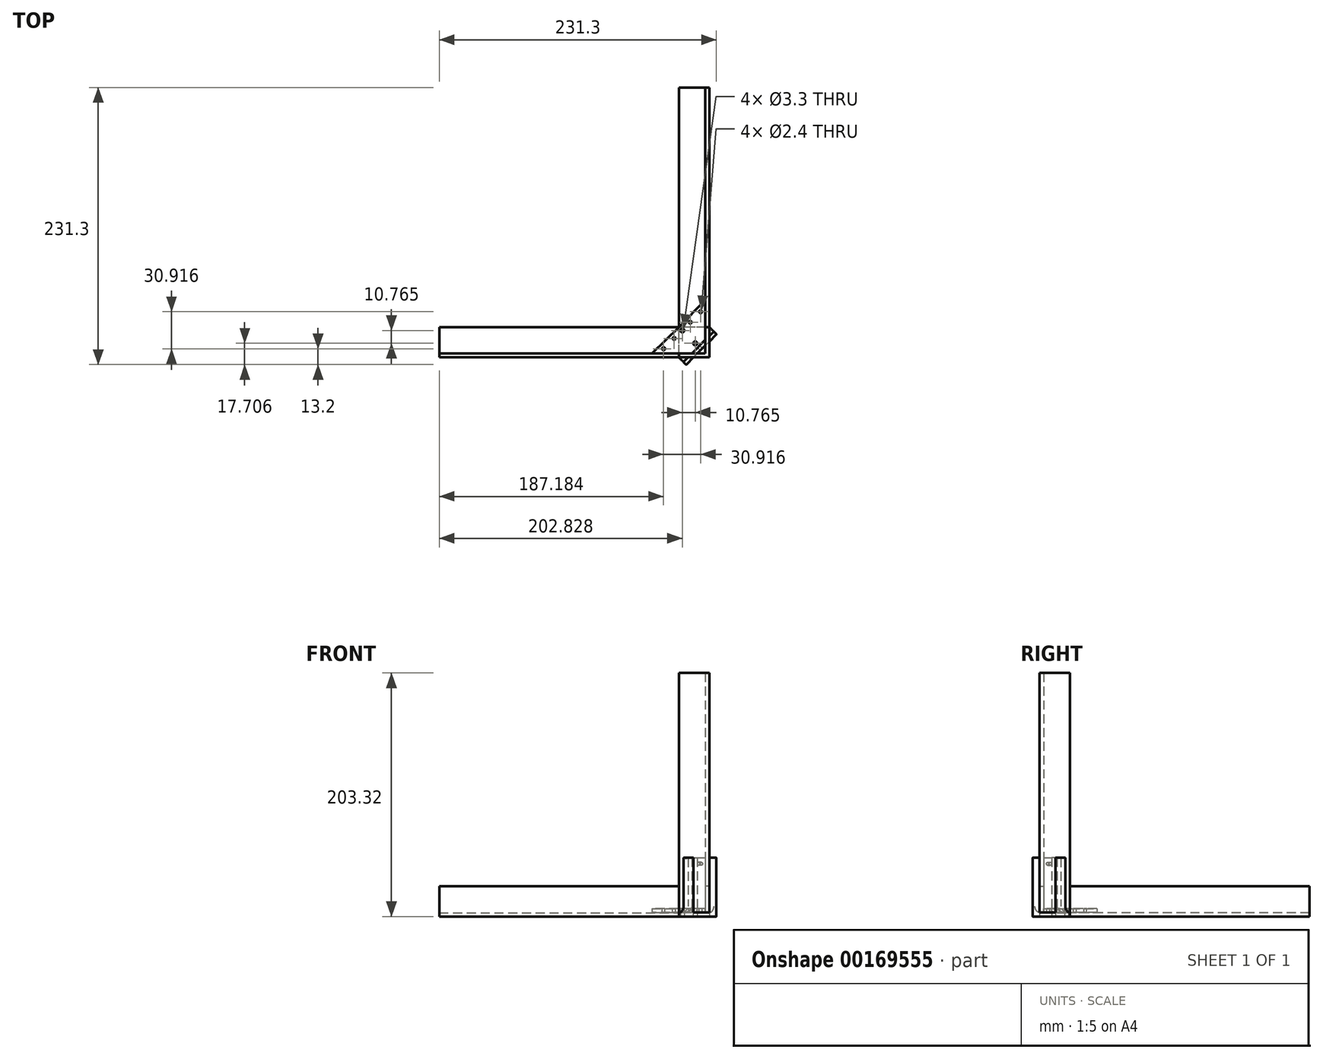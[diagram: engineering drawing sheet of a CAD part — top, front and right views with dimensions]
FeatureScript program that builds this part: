
annotation { "Feature Type Name" : "Feature", "Feature Type Description" : "" }
export const myFeature = defineFeature(function(context is Context, id is Id, definition is map)
    precondition{}
    {
        {
            assignVariable(context, id + "F0", {"name" : "EdgeLWidth", "anyValue" : 25.3 * mm});
        }
        {
            assignVariable(context, id + "F1", {"name" : "HolderLWidth", "anyValue" : 49 * mm});
        }
        {
            assignVariable(context, id + "F2", {"name" : "HolderLThickness", "anyValue" : 3.3 * mm});
        }
        {
            var Q0;
            Q0=qCreatedBy(makeId("Top.planeOp"),FACE);
            var sketch = newSketch(context, id + "F3", { "sketchPlane" : qUnion([Q0])});
            skLineSegment(sketch, "E0", {"start": v(-3.2, 9.89) * mm, "end": v(-6.54, 6.54) * mm});
            skLineSegment(sketch, "E1", {"start": v(-8.88, 8.88) * mm, "end": v(-3.2, 14.56) * mm});
            skLineSegment(sketch, "E2", {"start": v(-3.2, 14.56) * mm, "end": v(-3.2, 9.89) * mm});
            skLineSegment(sketch, "E3", {"start": v(0, 13.09) * mm, "end": v(0, 17.76) * mm});
            skLineSegment(sketch, "E4", {"start": v(0, 17.76) * mm, "end": v(3.77, 21.53) * mm});
            skLineSegment(sketch, "E5", {"start": v(3.77, 21.53) * mm, "end": v(6.1, 19.2) * mm});
            skLineSegment(sketch, "E6", {"start": v(6.1, 19.2) * mm, "end": v(0, 13.09) * mm});
            skLineSegment(sketch, "E7", {"start": v(0, 0) * mm, "end": v(-77.69, 77.69) * mm, "construction": true});
            skLineSegment(sketch, "E8", {"start": v(-77.76, 0) * mm, "end": v(0, 0) * mm, "construction": true});
            skLineSegment(sketch, "E9", {"start": v(0, 0) * mm, "end": v(0, 78.06) * mm, "construction": true});
            skLineSegment(sketch, "E10", {"start": v(6.1, 19.2) * mm, "end": v(-6.54, 6.54) * mm});
            skLineSegment(sketch, "E11.MirrorCS", {"start": v(-19.2, -6.1) * mm, "end": v(-13.09, 0) * mm});
            skLineSegment(sketch, "E12.MirrorCS", {"start": v(-9.89, 3.2) * mm, "end": v(-6.54, 6.54) * mm});
            skLineSegment(sketch, "E13.MirrorCS", {"start": v(-17.76, 0) * mm, "end": v(-21.53, -3.77) * mm});
            skLineSegment(sketch, "E14.MirrorCS", {"start": v(-8.88, 8.88) * mm, "end": v(-14.56, 3.2) * mm});
            skLineSegment(sketch, "E15.MirrorCS", {"start": v(-13.09, 0) * mm, "end": v(-17.76, 0) * mm});
            skLineSegment(sketch, "E16.MirrorCS", {"start": v(-21.53, -3.77) * mm, "end": v(-19.2, -6.1) * mm});
            skLineSegment(sketch, "E17.MirrorCS", {"start": v(-19.2, -6.1) * mm, "end": v(-6.54, 6.54) * mm});
            skLineSegment(sketch, "E18.MirrorCS", {"start": v(-14.56, 3.2) * mm, "end": v(-9.89, 3.2) * mm});
            skPoint(sketch, "E19", {"position": v(-11.7, 11.7) * mm});
            skPoint(sketch, "E20", {"position": v(-22.47, 22.47) * mm});
            skLineSegment(sketch, "E21", {"start": v(3.77, 21.53) * mm, "end": v(0, 25.3) * mm});
            skLineSegment(sketch, "E22", {"start": v(0, 25.3) * mm, "end": v(-25.3, 25.3) * mm});
            skLineSegment(sketch, "E23", {"start": v(-25.3, 25.3) * mm, "end": v(-25.3, 0) * mm});
            skLineSegment(sketch, "E24", {"start": v(-25.3, 0) * mm, "end": v(-21.53, -3.77) * mm});
            skSolve(sketch);
        }
        {
            var Q0;
            Q0=qSketchRegion(id+"F3",true);
            extrude(context, id + "F4", {"entities" : qUnion([Q0]), "depth" : getVariable(context, 'HolderLThickness')});
        }
        {
            var Q0;
            {var subQ0=sQuery(id+"F3.wireOp",EDGE,"E3");Q0=makeQuery(id+"F3.imprint","IMPRINT",FACE,{"disambiguationData":[TD([[makeQuery(id+"F3.imprint","IMPRINT",EDGE,{"derivedFrom":subQ0}),-1.0]])]});}
            var Q1;
            Q1=makeQuery(id+"F3.imprint","IMPRINT",FACE,{"disambiguationData":[TD([[makeQuery(id+"F3.imprint","IMPRINT",EDGE,{"derivedFrom":sQuery(id+"F3.wireOp",EDGE,"E1")}),-1.0]])]});
            var Q2;
            Q2=makeQuery(id+"F3.imprint","IMPRINT",FACE,{"disambiguationData":[TD([[makeQuery(id+"F3.imprint","IMPRINT",EDGE,{"derivedFrom":sQuery(id+"F3.wireOp",EDGE,"E13.MirrorCS")}),1.0]])]});
            extrude(context, id + "F5", {"entities" : qUnion([Q0, Q1, Q2]), "operationType" : NewBodyOperationType.ADD, "depth" : getVariable(context, 'HolderLWidth')});
        }
        {
            var Q0;
            Q0=sQuery(id+"F3.wireOp",VERTEX,"E19");
            var Q1;
            Q1=sQuery(id+"F3.wireOp",VERTEX,"E20");
            var Q2;
            Q2=makeQuery(id+"F4.opExtrude","SWEPT_BODY",BODY,{"disambiguationData":[OSD([sQuery(id+"F3.wireOp",EDGE,"E5"),sQuery(id+"F3.wireOp",EDGE,"o0lL32gh-OSn4-Vle3-xUkx-KtaRwmzb5psM"),sQuery(id+"F3.wireOp",EDGE,"DVCsqTKq-KYus-YFW3-ZN70-3ISmhOG0B1KU"),sQuery(id+"F3.wireOp",EDGE,"E10"),sQuery(id+"F3.wireOp",EDGE,"bed3d973-7b21-4a2b-b050-399250b5e04a2.MirrorCS"),sQuery(id+"F3.wireOp",EDGE,"bed3d973-7b21-4a2b-b050-399250b5e04a6.MirrorCS"),sQuery(id+"F3.wireOp",EDGE,"E16.MirrorCS"),sQuery(id+"F3.wireOp",EDGE,"E17.MirrorCS")])]});
            hole(context, id + "F6", {"style" : HoleStyle.SIMPLE, "endStyle" : HoleEndStyle.THROUGH, "oppositeDirection" : true, "standardTappedOrClearance" : lookupTablePath({ "standard" : "ISO", "fit" : "Normal", "size" : "M3", "type" : "Clearance" }), "standardBlindInLast" : lookupTablePath({ "fit" : "Standard", "standard" : "ISO", "size" : "M3", "type" : "Clearance" }), "holeDiameter" : 3.3 * mm, "startFromSketch" : true, "locations" : qUnion([Q0, Q1]), "scope" : qUnion([Q2]), "isTappedThrough" : true});
        }
        {
            var Q0;
            Q0=makeQuery(id+"F5.opExtrude","SWEPT_FACE",FACE,{"disambiguationData":[OSD([sQuery(id+"F3.wireOp",EDGE,"E1"),sQuery(id+"F3.wireOp",EDGE,"E14.MirrorCS")])]});
            var sketch = newSketch(context, id + "F7", { "sketchPlane" : qUnion([Q0])});
            skLineSegment(sketch, "E25", {"start": v(0, 49) * mm, "end": v(0, 0) * mm, "construction": true});
            skPoint(sketch, "E26", {"position": v(0, 44) * mm});
            skSolve(sketch);
        }
        {
            var Q0;
            Q0=sQuery(id+"F7.wireOp",VERTEX,"E26");
            var Q1;
            Q1=makeQuery(id+"F4.opExtrude","SWEPT_BODY",BODY,{"disambiguationData":[OSD([sQuery(id+"F3.wireOp",EDGE,"E5"),sQuery(id+"F3.wireOp",EDGE,"o0lL32gh-OSn4-Vle3-xUkx-KtaRwmzb5psM"),sQuery(id+"F3.wireOp",EDGE,"DVCsqTKq-KYus-YFW3-ZN70-3ISmhOG0B1KU"),sQuery(id+"F3.wireOp",EDGE,"E10"),sQuery(id+"F3.wireOp",EDGE,"bed3d973-7b21-4a2b-b050-399250b5e04a2.MirrorCS"),sQuery(id+"F3.wireOp",EDGE,"bed3d973-7b21-4a2b-b050-399250b5e04a6.MirrorCS"),sQuery(id+"F3.wireOp",EDGE,"E16.MirrorCS"),sQuery(id+"F3.wireOp",EDGE,"E17.MirrorCS")])]});
            hole(context, id + "F8", {"style" : HoleStyle.SIMPLE, "endStyle" : HoleEndStyle.THROUGH, "standardTappedOrClearance" : lookupTablePath({ "standard" : "ISO", "engagement" : "75%", "pitch" : "0.6 mm", "size" : "M3", "type" : "Tapped" }), "standardBlindInLast" : lookupTablePath({ "standard" : "ISO", "engagement" : "75%", "pitch" : "0.6 mm", "size" : "M3", "type" : "Tapped" }), "holeDiameter" : 2.4 * mm, "startFromSketch" : true, "locations" : qUnion([Q0]), "scope" : qUnion([Q1]), "isTappedThrough" : true, "showTappedDepth" : true});
        }
        {
            var Q0;
            {var subQ0=sQuery(id+"F3.wireOp",EDGE,"E10");var subQ1=sQuery(id+"F3.wireOp",EDGE,"E5");Q0=makeQuery(id+"F5.boolean.opBoolean","MERGE",EDGE,{"derivedFrom":[makeQuery(id+"F4.opExtrude","SWEPT_EDGE",EDGE,{"disambiguationData":[OSD([subQ1,subQ0])]}),makeQuery(id+"F5.opExtrude","SWEPT_EDGE",EDGE,{"disambiguationData":[OSD([subQ1,subQ0])]})]});}
            var Q1;
            Q1=makeQuery(id+"F5.opExtrude","SWEPT_EDGE",EDGE,{"disambiguationData":[OSD([sQuery(id+"F3.wireOp",EDGE,"E4"),sQuery(id+"F3.wireOp",EDGE,"E5"),sQuery(id+"F3.wireOp",EDGE,"o0lL32gh-OSn4-Vle3-xUkx-KtaRwmzb5psM")])]});
            var Q2;
            Q2=makeQuery(id+"F5.opExtrude","CAP_EDGE",EDGE,{"disambiguationData":[OSD([sQuery(id+"F3.wireOp",EDGE,"E5")])],"isStart":false});
            var Q3;
            Q3=makeQuery(id+"F5.opExtrude","CAP_EDGE",EDGE,{"disambiguationData":[OSD([sQuery(id+"F3.wireOp",EDGE,"E10")])],"isStart":false});
            var Q4;
            Q4=makeQuery(id+"F5.opExtrude","CAP_EDGE",EDGE,{"disambiguationData":[OSD([sQuery(id+"F3.wireOp",EDGE,"E4")])],"isStart":false});
            var Q5;
            Q5=makeQuery(id+"F5.opExtrude","CAP_EDGE",EDGE,{"disambiguationData":[OSD([sQuery(id+"F3.wireOp",EDGE,"E17.MirrorCS")])],"isStart":false});
            var Q6;
            Q6=makeQuery(id+"F5.opExtrude","CAP_EDGE",EDGE,{"disambiguationData":[OSD([sQuery(id+"F3.wireOp",EDGE,"E13.MirrorCS")])],"isStart":false});
            var Q7;
            Q7=makeQuery(id+"F5.opExtrude","CAP_EDGE",EDGE,{"disambiguationData":[OSD([sQuery(id+"F3.wireOp",EDGE,"E16.MirrorCS")])],"isStart":false});
            var Q8;
            {var subQ0=sQuery(id+"F3.wireOp",EDGE,"E17.MirrorCS");var subQ1=sQuery(id+"F3.wireOp",EDGE,"E16.MirrorCS");Q8=makeQuery(id+"F5.boolean.opBoolean","MERGE",EDGE,{"derivedFrom":[makeQuery(id+"F4.opExtrude","SWEPT_EDGE",EDGE,{"disambiguationData":[OSD([subQ1,subQ0])]}),makeQuery(id+"F5.opExtrude","SWEPT_EDGE",EDGE,{"disambiguationData":[OSD([subQ1,subQ0])]})]});}
            var Q9;
            Q9=makeQuery(id+"F5.opExtrude","SWEPT_EDGE",EDGE,{"disambiguationData":[OSD([sQuery(id+"F3.wireOp",EDGE,"bed3d973-7b21-4a2b-b050-399250b5e04a2.MirrorCS"),sQuery(id+"F3.wireOp",EDGE,"E13.MirrorCS"),sQuery(id+"F3.wireOp",EDGE,"E16.MirrorCS")])]});
            fillet(context, id + "F9", {"entities" : qUnion([Q0, Q1, Q2, Q3, Q4, Q5, Q6, Q7, Q8, Q9]), "radius" : .25 * mm, "tangentPropagation" : true, "allowEdgeOverflow" : false});
        }
        {
            var Q0;
            Q0=makeQuery(id+"F4.opExtrude","CAP_FACE",FACE,{"disambiguationData":[OSD([sQuery(id+"F3.wireOp",EDGE,"E5"),sQuery(id+"F3.wireOp",EDGE,"o0lL32gh-OSn4-Vle3-xUkx-KtaRwmzb5psM"),sQuery(id+"F3.wireOp",EDGE,"DVCsqTKq-KYus-YFW3-ZN70-3ISmhOG0B1KU"),sQuery(id+"F3.wireOp",EDGE,"E10"),sQuery(id+"F3.wireOp",EDGE,"bed3d973-7b21-4a2b-b050-399250b5e04a2.MirrorCS"),sQuery(id+"F3.wireOp",EDGE,"bed3d973-7b21-4a2b-b050-399250b5e04a6.MirrorCS"),sQuery(id+"F3.wireOp",EDGE,"E16.MirrorCS"),sQuery(id+"F3.wireOp",EDGE,"E17.MirrorCS")])],"isStart":false});
            var sketch = newSketch(context, id + "F10", { "sketchPlane" : qUnion([Q0])});
            skLineSegment(sketch, "E27", {"start": v(0, 0) * mm, "end": v(0, 25.3) * mm});
            skLineSegment(sketch, "E28", {"start": v(-3.2, 25.3) * mm, "end": v(-3.2, 3.2) * mm});
            skLineSegment(sketch, "E29", {"start": v(-3.2, 3.2) * mm, "end": v(-25.3, 3.2) * mm});
            skLineSegment(sketch, "E30", {"start": v(-25.3, 3.2) * mm, "end": v(-25.3, 0) * mm});
            skLineSegment(sketch, "E31", {"start": v(-25.3, 0) * mm, "end": v(0, 0) * mm});
            skLineSegment(sketch, "E32", {"start": v(-3.2, 25.3) * mm, "end": v(0, 25.3) * mm});
            skSolve(sketch);
        }
        {
            var Q0;
            Q0=qSketchRegion(id+"F10",true);
            extrude(context, id + "F11", {"entities" : qUnion([Q0]), "depth" : 200 * mm});
        }
        {
            var Q0;
            Q0=qCreatedBy(makeId("Right.planeOp"),FACE);
            var sketch = newSketch(context, id + "F12", { "sketchPlane" : qUnion([Q0])});
            skLineSegment(sketch, "E33", {"start": v(0, -0.02) * mm, "end": v(0, 25.28) * mm});
            skLineSegment(sketch, "E34", {"start": v(0, 25.28) * mm, "end": v(3.2, 25.28) * mm});
            skLineSegment(sketch, "E35", {"start": v(3.2, 25.28) * mm, "end": v(3.2, 3.18) * mm});
            skLineSegment(sketch, "E36", {"start": v(3.2, 3.18) * mm, "end": v(25.3, 3.18) * mm});
            skLineSegment(sketch, "E37", {"start": v(25.3, 3.18) * mm, "end": v(25.3, -0.02) * mm});
            skLineSegment(sketch, "E38", {"start": v(0, -0.02) * mm, "end": v(25.3, -0.02) * mm});
            skSolve(sketch);
        }
        {
            var Q0;
            Q0=qSketchRegion(id+"F12",true);
            extrude(context, id + "F13", {"entities" : qUnion([Q0]), "oppositeDirection" : true, "depth" : 200 * mm});
        }
        {
            var Q0;
            Q0=makeQuery(id+"F13.opExtrude","SWEPT_BODY",BODY,{"disambiguationData":[OSD([sQuery(id+"F12.wireOp",EDGE,"E33"),sQuery(id+"F12.wireOp",EDGE,"E34"),sQuery(id+"F12.wireOp",EDGE,"E35"),sQuery(id+"F12.wireOp",EDGE,"E36"),sQuery(id+"F12.wireOp",EDGE,"E37"),sQuery(id+"F12.wireOp",EDGE,"E38")])]});
            var Q1;
            Q1=makeQuery(id+"F13.opExtrude","SWEPT_EDGE",EDGE,{"disambiguationData":[OSD([sQuery(id+"F12.wireOp",EDGE,"E36"),sQuery(id+"F12.wireOp",EDGE,"E37")])]});
            transform(context, id + "F14", {"entities" : qUnion([Q0]), "transformType" : TransformType.TRANSLATION_3D, "dx" : -getVariable(context, 'EdgeLWidth'), "dy" : 0 * mm, "dz" : 0 * mm, "makeCopy" : false});
        }
        {
            var Q0;
            Q0=sQuery(id+"F3.wireOp",EDGE,"E7");
            var Q1;
            Q1=makeQuery(id+"F11.opExtrude","SWEPT_EDGE",EDGE,{"disambiguationData":[OSD([sQuery(id+"F10.wireOp",EDGE,"E27"),sQuery(id+"F10.wireOp",EDGE,"E31")])]});
            cPlane(context, id + "F15", {"entities" : qUnion([Q0, Q1]), "cplaneType" : CPlaneType.LINE_ANGLE, "offset" : 25 * mm, "angle" : 180 * degree, "width" : 150 * mm, "height" : 150 * mm});
        }
        {
            var Q0;
            Q0=makeQuery(id+"F13.opExtrude","SWEPT_BODY",BODY,{"disambiguationData":[OSD([sQuery(id+"F12.wireOp",EDGE,"E33"),sQuery(id+"F12.wireOp",EDGE,"E34"),sQuery(id+"F12.wireOp",EDGE,"E35"),sQuery(id+"F12.wireOp",EDGE,"E36"),sQuery(id+"F12.wireOp",EDGE,"E37"),sQuery(id+"F12.wireOp",EDGE,"E38")])]});
            var Q1;
            Q1=qCreatedBy(id+"F15.planeOp",FACE);
            mirror(context, id + "F16", {"entities" : qUnion([Q0]), "mirrorPlane" : qUnion([Q1])});
        }
        {
            var Q0;
            Q0=makeQuery(id+"F4.opExtrude","CAP_FACE",FACE,{"disambiguationData":[OSD([sQuery(id+"F3.wireOp",EDGE,"E5"),sQuery(id+"F3.wireOp",EDGE,"E10"),sQuery(id+"F3.wireOp",EDGE,"E16.MirrorCS"),sQuery(id+"F3.wireOp",EDGE,"E17.MirrorCS"),sQuery(id+"F3.wireOp",EDGE,"E21"),sQuery(id+"F3.wireOp",EDGE,"E22"),sQuery(id+"F3.wireOp",EDGE,"E23"),sQuery(id+"F3.wireOp",EDGE,"E24")])],"isStart":false});
            var sketch = newSketch(context, id + "F17", { "sketchPlane" : qUnion([Q0])});
            skLineSegment(sketch, "E39", {"start": v(-14.56, 3.2) * mm, "end": v(-47.94, 3.2) * mm});
            skLineSegment(sketch, "E40", {"start": v(-47.94, 3.2) * mm, "end": v(-25.3, 25.3) * mm});
            skLineSegment(sketch, "E41", {"start": v(-8.88, 8.88) * mm, "end": v(-14.56, 3.2) * mm});
            skLineSegment(sketch, "E42.MirrorCS", {"start": v(-8.88, 8.88) * mm, "end": v(-3.2, 14.56) * mm});
            skLineSegment(sketch, "E43.MirrorCS", {"start": v(-3.2, 14.56) * mm, "end": v(-3.2, 47.94) * mm});
            skLineSegment(sketch, "E44.MirrorCS", {"start": v(-3.2, 47.94) * mm, "end": v(-25.3, 25.3) * mm});
            skSolve(sketch);
        }
        {
            var Q0;
            Q0 = qSketchRegion(id + "F17", true);
            extrude(context, id + "F18", {"entities" : qUnion([Q0]), "depth" : getVariable(context, 'HolderLThickness')});
        }
        {
            var Q0;
            Q0=makeQuery(id+"F18.opExtrude","CAP_FACE",FACE,{"disambiguationData":[OSD([sQuery(id+"F17.wireOp",EDGE,"E39"),sQuery(id+"F17.wireOp",EDGE,"E40"),sQuery(id+"F17.wireOp",EDGE,"E41"),sQuery(id+"F17.wireOp",EDGE,"E42.MirrorCS"),sQuery(id+"F17.wireOp",EDGE,"E43.MirrorCS"),sQuery(id+"F17.wireOp",EDGE,"E44.MirrorCS")])],"isStart":false});
            var sketch = newSketch(context, id + "F19", { "sketchPlane" : qUnion([Q0])});
            skPoint(sketch, "E45", {"position": v(-22.47, 22.47) * mm});
            skPoint(sketch, "E46", {"position": v(-11.7, 11.7) * mm});
            skPoint(sketch, "E47", {"position": v(-29.3, 15.8) * mm});
            skPoint(sketch, "E48", {"position": v(-38.12, 7.2) * mm});
            skPoint(sketch, "E49.MirrorP", {"position": v(-15.8, 29.3) * mm});
            skPoint(sketch, "E50.MirrorP", {"position": v(-7.2, 38.12) * mm});
            skSolve(sketch);
        }
        {
            var Q0;
            Q0=sQuery(id+"F19.wireOp",VERTEX,"E45");
            var Q1;
            Q1=sQuery(id+"F19.wireOp",VERTEX,"E46");
            var Q2;
            Q2=makeQuery(id+"F18.opExtrude","SWEPT_BODY",BODY,{"disambiguationData":[OSD([sQuery(id+"F17.wireOp",EDGE,"E39"),sQuery(id+"F17.wireOp",EDGE,"E40"),sQuery(id+"F17.wireOp",EDGE,"E41"),sQuery(id+"F17.wireOp",EDGE,"E42.MirrorCS"),sQuery(id+"F17.wireOp",EDGE,"E43.MirrorCS"),sQuery(id+"F17.wireOp",EDGE,"E44.MirrorCS")])]});
            hole(context, id + "F20", {"style" : HoleStyle.SIMPLE, "endStyle" : HoleEndStyle.THROUGH, "standardTappedOrClearance" : lookupTablePath({ "standard" : "ISO", "fit" : "Normal", "size" : "M3", "type" : "Clearance" }), "standardBlindInLast" : lookupTablePath({ "fit" : "Standard", "standard" : "ISO", "size" : "M3", "type" : "Clearance" }), "holeDiameter" : 3.3 * mm, "startFromSketch" : true, "locations" : qUnion([Q0, Q1]), "scope" : qUnion([Q2]), "isTappedThrough" : true});
        }
        {
            var Q0;
            Q0=sQuery(id+"F19.wireOp",VERTEX,"E48");
            var Q1;
            Q1=sQuery(id+"F19.wireOp",VERTEX,"E47");
            var Q2;
            Q2=sQuery(id+"F19.wireOp",VERTEX,"E49.MirrorP");
            var Q3;
            Q3=sQuery(id+"F19.wireOp",VERTEX,"E50.MirrorP");
            var Q4;
            Q4=makeQuery(id+"F18.opExtrude","SWEPT_BODY",BODY,{"disambiguationData":[OSD([sQuery(id+"F17.wireOp",EDGE,"E39"),sQuery(id+"F17.wireOp",EDGE,"E40"),sQuery(id+"F17.wireOp",EDGE,"E41"),sQuery(id+"F17.wireOp",EDGE,"E42.MirrorCS"),sQuery(id+"F17.wireOp",EDGE,"E43.MirrorCS"),sQuery(id+"F17.wireOp",EDGE,"E44.MirrorCS")])]});
            hole(context, id + "F21", {"style" : HoleStyle.SIMPLE, "endStyle" : HoleEndStyle.THROUGH, "standardTappedOrClearance" : lookupTablePath({ "standard" : "ISO", "engagement" : "75%", "pitch" : "0.6 mm", "size" : "M3", "type" : "Tapped" }), "standardBlindInLast" : lookupTablePath({ "standard" : "ISO", "engagement" : "75%", "pitch" : "0.6 mm", "size" : "M3", "type" : "Tapped" }), "holeDiameter" : 2.4 * mm, "locations" : qUnion([Q0, Q1, Q2, Q3]), "scope" : qUnion([Q4]), "isTappedThrough" : true, "showTappedDepth" : true});
        }
        {
            var Q0;
            Q0=makeQuery(id+"F18.opExtrude","CAP_EDGE",EDGE,{"disambiguationData":[OSD([sQuery(id+"F17.wireOp",EDGE,"E41"),sQuery(id+"F17.wireOp",EDGE,"E42.MirrorCS")])],"isStart":true});
            var Q1;
            Q1=makeQuery(id+"F5.boolean.opBoolean","INTERSECT",EDGE,{"derivedFrom":[makeQuery(id+"F4.opExtrude","CAP_FACE",FACE,{"disambiguationData":[OSD([sQuery(id+"F3.wireOp",EDGE,"E5"),sQuery(id+"F3.wireOp",EDGE,"E10"),sQuery(id+"F3.wireOp",EDGE,"E16.MirrorCS"),sQuery(id+"F3.wireOp",EDGE,"E17.MirrorCS"),sQuery(id+"F3.wireOp",EDGE,"E21"),sQuery(id+"F3.wireOp",EDGE,"E22"),sQuery(id+"F3.wireOp",EDGE,"E23"),sQuery(id+"F3.wireOp",EDGE,"E24")])],"isStart":false}),makeQuery(id+"F5.opExtrude","SWEPT_FACE",FACE,{"disambiguationData":[OSD([sQuery(id+"F3.wireOp",EDGE,"E1"),sQuery(id+"F3.wireOp",EDGE,"E14.MirrorCS")])]})]});
            var Q2;
            Q2=makeQuery(id+"F5.boolean.opBoolean","INTERSECT",EDGE,{"derivedFrom":[makeQuery(id+"F4.opExtrude","CAP_FACE",FACE,{"disambiguationData":[OSD([sQuery(id+"F3.wireOp",EDGE,"E5"),sQuery(id+"F3.wireOp",EDGE,"E10"),sQuery(id+"F3.wireOp",EDGE,"E16.MirrorCS"),sQuery(id+"F3.wireOp",EDGE,"E17.MirrorCS"),sQuery(id+"F3.wireOp",EDGE,"E21"),sQuery(id+"F3.wireOp",EDGE,"E22"),sQuery(id+"F3.wireOp",EDGE,"E23"),sQuery(id+"F3.wireOp",EDGE,"E24")])],"isStart":false}),makeQuery(id+"F5.opExtrude","SWEPT_FACE",FACE,{"disambiguationData":[OSD([sQuery(id+"F3.wireOp",EDGE,"E13.MirrorCS")])]})]});
            var Q3;
            Q3=makeQuery(id+"F5.boolean.opBoolean","INTERSECT",EDGE,{"derivedFrom":[makeQuery(id+"F4.opExtrude","CAP_FACE",FACE,{"disambiguationData":[OSD([sQuery(id+"F3.wireOp",EDGE,"E5"),sQuery(id+"F3.wireOp",EDGE,"E10"),sQuery(id+"F3.wireOp",EDGE,"E16.MirrorCS"),sQuery(id+"F3.wireOp",EDGE,"E17.MirrorCS"),sQuery(id+"F3.wireOp",EDGE,"E21"),sQuery(id+"F3.wireOp",EDGE,"E22"),sQuery(id+"F3.wireOp",EDGE,"E23"),sQuery(id+"F3.wireOp",EDGE,"E24")])],"isStart":false}),makeQuery(id+"F5.opExtrude","SWEPT_FACE",FACE,{"disambiguationData":[OSD([sQuery(id+"F3.wireOp",EDGE,"E4")])]})]});
            fillet(context, id + "F22", {"entities" : qUnion([Q0, Q1, Q2, Q3]), "radius" : 5 * mm, "tangentPropagation" : true, "allowEdgeOverflow" : false});
        }
    });
